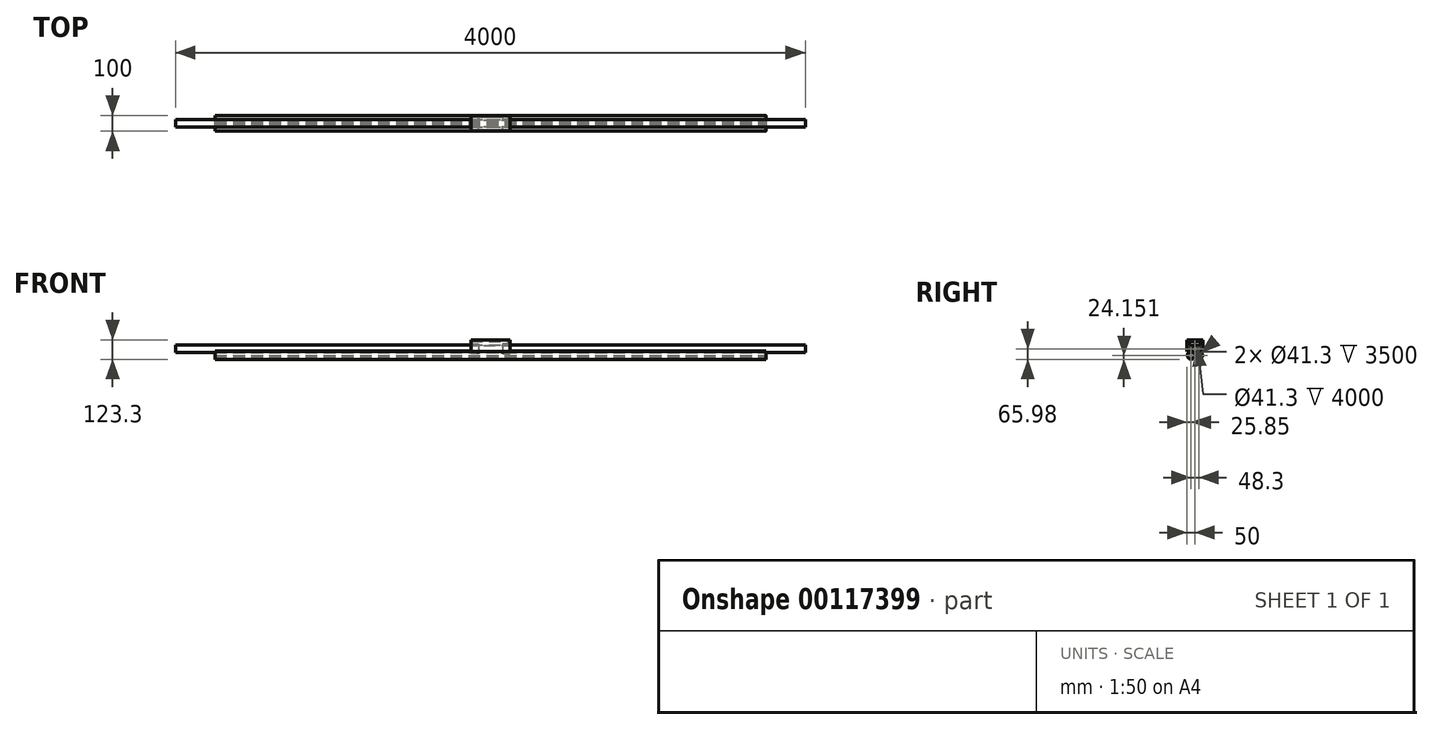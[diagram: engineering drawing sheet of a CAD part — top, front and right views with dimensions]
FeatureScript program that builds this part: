
annotation { "Feature Type Name" : "Feature", "Feature Type Description" : "" }
export const myFeature = defineFeature(function(context is Context, id is Id, definition is map)
    precondition{}
    {
        {
            var Q0;
            Q0=qCreatedBy(makeId("Right.planeOp"),FACE);
            var sketch = newSketch(context, id + "F0", { "sketchPlane" : qUnion([Q0])});
            skArc(sketch, "E0", {"start": v(-0.09, 0) * mm, "mid": v(0, 0) * mm, "end": v(0.09, 0) * mm});
            skArc(sketch, "E1", {"start": v(3.28, -5.53) * mm, "mid": v(3.24, -5.6) * mm, "end": v(3.2, -5.68) * mm});
            skArc(sketch, "E2", {"start": v(-24.06, 6.47) * mm, "mid": v(-45.06, -29.75) * mm, "end": v(-3.2, -29.68) * mm});
            skLineSegment(sketch, "E3", {"start": v(0, 24.15) * mm, "end": v(-24.15, -17.68) * mm, "construction": true});
            skLineSegment(sketch, "E4", {"start": v(-20.87, 12) * mm, "end": v(-24.06, 6.47) * mm});
            skLineSegment(sketch, "E5", {"start": v(-1.68, -2.76) * mm, "end": v(-22.47, 9.24) * mm, "construction": true});
            skLineSegment(sketch, "E6", {"start": v(24.15, -17.68) * mm, "end": v(0, 24.15) * mm, "construction": true});
            skLineSegment(sketch, "E7", {"start": v(24.15, -17.68) * mm, "end": v(-24.15, -17.68) * mm, "construction": true});
            skLineSegment(sketch, "E8", {"start": v(20.87, 12) * mm, "end": v(24.06, 6.47) * mm});
            skLineSegment(sketch, "E9", {"start": v(22.47, 9.24) * mm, "end": v(1.68, -2.76) * mm, "construction": true});
            skArc(sketch, "E10.trimOffspring", {"start": v(20.87, 12) * mm, "mid": v(0, 48.3) * mm, "end": v(-20.87, 12) * mm});
            skLineSegment(sketch, "E11", {"start": v(3.2, -29.68) * mm, "end": v(-3.2, -29.68) * mm});
            skLineSegment(sketch, "E12", {"start": v(0, -5.68) * mm, "end": v(0, -29.68) * mm, "construction": true});
            skArc(sketch, "E13.trimOffspring", {"start": v(-3.2, -5.68) * mm, "mid": v(-3.24, -5.6) * mm, "end": v(-3.28, -5.53) * mm});
            skArc(sketch, "E14.trimOffspring", {"start": v(3.2, -29.68) * mm, "mid": v(45.06, -29.75) * mm, "end": v(24.06, 6.47) * mm});
            skCircle(sketch, "E15", {"center": v(24.15, -17.68) * mm, "radius": 20.65 * mm});
            skCircle(sketch, "E16", {"center": v(-24.15, -17.68) * mm, "radius": 20.65 * mm});
            skCircle(sketch, "E17", {"center": v(0, 24.15) * mm, "radius": 20.65 * mm});
            skArc(sketch, "E18", {"start": v(0.09, 0) * mm, "mid": v(6.3, 0.83) * mm, "end": v(12.07, 3.24) * mm});
            skArc(sketch, "E19", {"start": v(3.28, -5.53) * mm, "mid": v(7.1, -0.57) * mm, "end": v(12.07, 3.24) * mm});
            skArc(sketch, "E20", {"start": v(-3.28, -5.53) * mm, "mid": v(-7.1, -0.57) * mm, "end": v(-12.08, 3.24) * mm});
            skArc(sketch, "E21", {"start": v(-0.09, 0) * mm, "mid": v(-6.3, 0.83) * mm, "end": v(-12.07, 3.24) * mm});
            skArc(sketch, "E22", {"start": v(-3.2, -5.68) * mm, "mid": v(-0.81, -11.47) * mm, "end": v(0, -17.68) * mm});
            skArc(sketch, "E23", {"start": v(3.2, -5.68) * mm, "mid": v(0.81, -11.47) * mm, "end": v(0, -17.68) * mm});
            skSolve(sketch);
        }
        {
            var Q0;
            Q0 = qSketchRegion(id + "F0", true);
            extrude(context, id + "F1", {"entities" : qUnion([Q0]), "oppositeDirection" : true, "depth" : 4000 * mm});
        }
        {
            var Q0;
            Q0=makeQuery(id+"F1.opExtrude","CAP_FACE",FACE,{"disambiguationData":[OSD([sQuery(id+"F0.wireOp",EDGE,"E0"),sQuery(id+"F0.wireOp",EDGE,"E1"),sQuery(id+"F0.wireOp",EDGE,"E2"),sQuery(id+"F0.wireOp",EDGE,"E4"),sQuery(id+"F0.wireOp",EDGE,"E8"),sQuery(id+"F0.wireOp",EDGE,"E10.trimOffspring"),sQuery(id+"F0.wireOp",EDGE,"E11"),sQuery(id+"F0.wireOp",EDGE,"E13.trimOffspring"),sQuery(id+"F0.wireOp",EDGE,"E14.trimOffspring"),sQuery(id+"F0.wireOp",EDGE,"E15"),sQuery(id+"F0.wireOp",EDGE,"E16"),sQuery(id+"F0.wireOp",EDGE,"E17"),sQuery(id+"F0.wireOp",EDGE,"E18"),sQuery(id+"F0.wireOp",EDGE,"E19"),sQuery(id+"F0.wireOp",EDGE,"E20"),sQuery(id+"F0.wireOp",EDGE,"E21"),sQuery(id+"F0.wireOp",EDGE,"E22"),sQuery(id+"F0.wireOp",EDGE,"E23")])],"isStart":false});
            var sketch = newSketch(context, id + "F2", { "sketchPlane" : qUnion([Q0])});
            skCircle(sketch, "E24", {"center": v(0, 24.15) * mm, "radius": 24.15 * mm});
            skLineSegment(sketch, "E25.bottom", {"start": v(-60.5, -47.47) * mm, "end": v(59.85, -47.47) * mm});
            skLineSegment(sketch, "E25.top", {"start": v(-60.5, 49.3) * mm, "end": v(59.85, 49.3) * mm});
            skLineSegment(sketch, "E25.left", {"start": v(-60.5, -47.47) * mm, "end": v(-60.5, 49.3) * mm});
            skLineSegment(sketch, "E25.right", {"start": v(59.85, -47.47) * mm, "end": v(59.85, 49.3) * mm});
            skSolve(sketch);
        }
        {
            var Q0;
            Q0 = qSketchRegion(id + "F2", true);
            extrude(context, id + "F3", {"entities" : qUnion([Q0]), "operationType" : NewBodyOperationType.REMOVE, "oppositeDirection" : true, "depth" : 250 * mm});
        }
        {
            var Q0;
            Q0=makeQuery(id+"F1.opExtrude","CAP_FACE",FACE,{"disambiguationData":[OSD([sQuery(id+"F0.wireOp",EDGE,"E0"),sQuery(id+"F0.wireOp",EDGE,"E1"),sQuery(id+"F0.wireOp",EDGE,"E2"),sQuery(id+"F0.wireOp",EDGE,"E4"),sQuery(id+"F0.wireOp",EDGE,"E8"),sQuery(id+"F0.wireOp",EDGE,"E10.trimOffspring"),sQuery(id+"F0.wireOp",EDGE,"E11"),sQuery(id+"F0.wireOp",EDGE,"E13.trimOffspring"),sQuery(id+"F0.wireOp",EDGE,"E14.trimOffspring"),sQuery(id+"F0.wireOp",EDGE,"E15"),sQuery(id+"F0.wireOp",EDGE,"E16"),sQuery(id+"F0.wireOp",EDGE,"E17"),sQuery(id+"F0.wireOp",EDGE,"E18"),sQuery(id+"F0.wireOp",EDGE,"E19"),sQuery(id+"F0.wireOp",EDGE,"E20"),sQuery(id+"F0.wireOp",EDGE,"E21"),sQuery(id+"F0.wireOp",EDGE,"E22"),sQuery(id+"F0.wireOp",EDGE,"E23")])],"isStart":true});
            var sketch = newSketch(context, id + "F4", { "sketchPlane" : qUnion([Q0])});
            skCircle(sketch, "E26", {"center": v(0, 24.15) * mm, "radius": 24.15 * mm});
            skLineSegment(sketch, "E27.bottom", {"start": v(-79.63, -50.96) * mm, "end": v(69.63, -50.96) * mm});
            skLineSegment(sketch, "E27.top", {"start": v(-79.63, 57.3) * mm, "end": v(69.63, 57.3) * mm});
            skLineSegment(sketch, "E27.left", {"start": v(-79.63, -50.96) * mm, "end": v(-79.63, 57.3) * mm});
            skLineSegment(sketch, "E27.right", {"start": v(69.63, -50.96) * mm, "end": v(69.63, 57.3) * mm});
            skSolve(sketch);
        }
        {
            var Q0;
            Q0 = qSketchRegion(id + "F4", true);
            extrude(context, id + "F5", {"entities" : qUnion([Q0]), "operationType" : NewBodyOperationType.REMOVE, "oppositeDirection" : true, "depth" : 250 * mm});
        }
        {
            var Q0;
            Q0=makeQuery(id+"F1.opExtrude","CAP_FACE",FACE,{"disambiguationData":[OSD([sQuery(id+"F0.wireOp",EDGE,"E0"),sQuery(id+"F0.wireOp",EDGE,"E1"),sQuery(id+"F0.wireOp",EDGE,"E2"),sQuery(id+"F0.wireOp",EDGE,"E4"),sQuery(id+"F0.wireOp",EDGE,"E8"),sQuery(id+"F0.wireOp",EDGE,"E10.trimOffspring"),sQuery(id+"F0.wireOp",EDGE,"E11"),sQuery(id+"F0.wireOp",EDGE,"E13.trimOffspring"),sQuery(id+"F0.wireOp",EDGE,"E14.trimOffspring"),sQuery(id+"F0.wireOp",EDGE,"E15"),sQuery(id+"F0.wireOp",EDGE,"E16"),sQuery(id+"F0.wireOp",EDGE,"E17"),sQuery(id+"F0.wireOp",EDGE,"E18"),sQuery(id+"F0.wireOp",EDGE,"E19"),sQuery(id+"F0.wireOp",EDGE,"E20"),sQuery(id+"F0.wireOp",EDGE,"E21"),sQuery(id+"F0.wireOp",EDGE,"E22"),sQuery(id+"F0.wireOp",EDGE,"E23")])],"isStart":false});
            cPlane(context, id + "F6", {"entities" : qUnion([Q0]), "cplaneType" : CPlaneType.OFFSET, "offset" : 0 * mm, "width" : 150 * mm, "height" : 150 * mm});
        }
        {
            var Q0;
            Q0=qCreatedBy(id+"F6.planeOp",FACE);
            var Q1;
            Q1=qCreatedBy(makeId("Right.planeOp"),FACE);
            cPlane(context, id + "F7", {"entities" : qUnion([Q0, Q1]), "cplaneType" : CPlaneType.MID_PLANE, "offset" : 25 * mm, "width" : 150 * mm, "height" : 150 * mm});
        }
        {
            var Q0;
            Q0=qCreatedBy(id+"F7.planeOp",FACE);
            var sketch = newSketch(context, id + "F8", { "sketchPlane" : qUnion([Q0])});
            skLineSegment(sketch, "E28", {"start": v(50, 81.47) * mm, "end": v(-50, 81.47) * mm});
            skLineSegment(sketch, "E29", {"start": v(-50, 81.47) * mm, "end": v(-50, 6.47) * mm});
            skLineSegment(sketch, "E30", {"start": v(-50, 6.47) * mm, "end": v(-40, 6.47) * mm});
            skLineSegment(sketch, "E31", {"start": v(-40, 6.47) * mm, "end": v(-40, 71.47) * mm});
            skLineSegment(sketch, "E32", {"start": v(-40, 71.47) * mm, "end": v(40, 71.47) * mm});
            skLineSegment(sketch, "E33", {"start": v(40, 71.47) * mm, "end": v(40, 6.47) * mm});
            skLineSegment(sketch, "E34", {"start": v(40, 6.47) * mm, "end": v(50, 6.47) * mm});
            skLineSegment(sketch, "E35", {"start": v(50, 6.47) * mm, "end": v(50, 81.47) * mm});
            skLineSegment(sketch, "E36", {"start": v(50, 6.47) * mm, "end": v(-50, 6.47) * mm, "construction": true});
            skLineSegment(sketch, "E37", {"start": v(0, 81.47) * mm, "end": v(0, 71.47) * mm, "construction": true});
            skSolve(sketch);
        }
        {
            var Q0;
            Q0 = qSketchRegion(id + "F8", true);
            extrude(context, id + "F9", {"entities" : qUnion([Q0]), "endBound" : BoundingType.SYMMETRIC, "depth" : 250 * mm});
        }
        {
            var Q0;
            Q0=makeQuery(id+"F9.opExtrude","SWEPT_FACE",FACE,{"disambiguationData":[OSD([sQuery(id+"F8.wireOp",EDGE,"E34")])]});
            var sketch = newSketch(context, id + "F10", { "sketchPlane" : qUnion([Q0])});
            skLineSegment(sketch, "E38.bottom", {"start": v(-2125, 40) * mm, "end": v(-2075, 40) * mm});
            skLineSegment(sketch, "E38.top", {"start": v(-2125, 25) * mm, "end": v(-2075, 25) * mm});
            skLineSegment(sketch, "E38.left", {"start": v(-2125, 40) * mm, "end": v(-2125, 25) * mm});
            skLineSegment(sketch, "E38.right", {"start": v(-2075, 40) * mm, "end": v(-2075, 25) * mm});
            skLineSegment(sketch, "E39.bottom", {"start": v(-1875, 40) * mm, "end": v(-1925, 40) * mm});
            skLineSegment(sketch, "E39.top", {"start": v(-1875, 25) * mm, "end": v(-1925, 25) * mm});
            skLineSegment(sketch, "E39.left", {"start": v(-1875, 40) * mm, "end": v(-1875, 25) * mm});
            skLineSegment(sketch, "E39.right", {"start": v(-1925, 40) * mm, "end": v(-1925, 25) * mm});
            skLineSegment(sketch, "E40.bottom", {"start": v(-1875, -40) * mm, "end": v(-1925, -40) * mm});
            skLineSegment(sketch, "E40.top", {"start": v(-1875, -25) * mm, "end": v(-1925, -25) * mm});
            skLineSegment(sketch, "E40.left", {"start": v(-1875, -40) * mm, "end": v(-1875, -25) * mm});
            skLineSegment(sketch, "E40.right", {"start": v(-1925, -40) * mm, "end": v(-1925, -25) * mm});
            skLineSegment(sketch, "E41.bottom", {"start": v(-2125, -40) * mm, "end": v(-2075, -40) * mm});
            skLineSegment(sketch, "E41.top", {"start": v(-2125, -25) * mm, "end": v(-2075, -25) * mm});
            skLineSegment(sketch, "E41.left", {"start": v(-2125, -40) * mm, "end": v(-2125, -25) * mm});
            skLineSegment(sketch, "E41.right", {"start": v(-2075, -40) * mm, "end": v(-2075, -25) * mm});
            skSolve(sketch);
        }
        {
            var Q0;
            Q0 = qSketchRegion(id + "F10", true);
            extrude(context, id + "F11", {"entities" : qUnion([Q0]), "operationType" : NewBodyOperationType.ADD, "oppositeDirection" : true, "depth" : 50 * mm});
        }
        {
            var Q0;
            Q0=makeQuery(id+"F11.opExtrude","SWEPT_FACE",FACE,{"disambiguationData":[OSD([sQuery(id+"F10.wireOp",EDGE,"E38.left")])]});
            var sketch = newSketch(context, id + "F12", { "sketchPlane" : qUnion([Q0])});
            skLineSegment(sketch, "E42", {"start": v(25, 6.47) * mm, "end": v(25, 2.95) * mm});
            skLineSegment(sketch, "E43", {"start": v(40, 6.47) * mm, "end": v(40, -4.44) * mm});
            skArc(sketch, "E44", {"start": v(25, 2.95) * mm, "mid": v(33.28, 0.84) * mm, "end": v(40, -4.44) * mm});
            skLineSegment(sketch, "E45", {"start": v(25, 6.47) * mm, "end": v(40, 6.47) * mm});
            skLineSegment(sketch, "E46", {"start": v(-40, 6.47) * mm, "end": v(-40, -4.44) * mm});
            skLineSegment(sketch, "E47", {"start": v(-25, 6.47) * mm, "end": v(-25, 2.95) * mm});
            skLineSegment(sketch, "E48", {"start": v(-40, 6.47) * mm, "end": v(-25, 6.47) * mm});
            skArc(sketch, "E49", {"start": v(-25, 2.95) * mm, "mid": v(-33.28, 0.84) * mm, "end": v(-40, -4.44) * mm});
            skSolve(sketch);
        }
        {
            var Q0;
            Q0 = qSketchRegion(id + "F12", true);
            var Q1;
            Q1=makeQuery(id+"F11.opExtrude","SWEPT_FACE",FACE,{"disambiguationData":[OSD([sQuery(id+"F10.wireOp",EDGE,"E38.right")])]});
            extrude(context, id + "F13", {"entities" : qUnion([Q0]), "endBound" : BoundingType.UP_TO_SURFACE, "oppositeDirection" : true, "endBoundEntityFace" : qUnion([Q1]), "depth" : 25 * mm});
        }
        {
            var Q0;
            Q0=makeQuery(id+"F11.opExtrude","SWEPT_FACE",FACE,{"disambiguationData":[OSD([sQuery(id+"F10.wireOp",EDGE,"E40.left")])]});
            var sketch = newSketch(context, id + "F14", { "sketchPlane" : qUnion([Q0])});
            skLineSegment(sketch, "E50", {"start": v(40, 6.47) * mm, "end": v(40, -4.44) * mm});
            skLineSegment(sketch, "E51", {"start": v(25, 6.47) * mm, "end": v(25, 2.95) * mm});
            skLineSegment(sketch, "E52", {"start": v(25, 6.47) * mm, "end": v(40, 6.47) * mm});
            skArc(sketch, "E53", {"start": v(25, 2.95) * mm, "mid": v(33.28, 0.84) * mm, "end": v(40, -4.44) * mm});
            skLineSegment(sketch, "E54", {"start": v(-40, 6.47) * mm, "end": v(-40, -4.44) * mm});
            skLineSegment(sketch, "E55", {"start": v(-25, 6.47) * mm, "end": v(-25, 2.95) * mm});
            skArc(sketch, "E56", {"start": v(-25, 2.95) * mm, "mid": v(-33.28, 0.84) * mm, "end": v(-40, -4.44) * mm});
            skLineSegment(sketch, "E57", {"start": v(-40, 6.47) * mm, "end": v(-25, 6.47) * mm});
            skSolve(sketch);
        }
        {
            var Q0;
            Q0 = qSketchRegion(id + "F14", true);
            var Q1;
            Q1=makeQuery(id+"F11.opExtrude","SWEPT_FACE",FACE,{"disambiguationData":[OSD([sQuery(id+"F10.wireOp",EDGE,"E40.right")])]});
            extrude(context, id + "F15", {"entities" : qUnion([Q0]), "endBound" : BoundingType.UP_TO_SURFACE, "oppositeDirection" : true, "endBoundEntityFace" : qUnion([Q1]), "depth" : 25 * mm});
        }
    });
